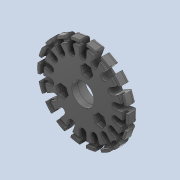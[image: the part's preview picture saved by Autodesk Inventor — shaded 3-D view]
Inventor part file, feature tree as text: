
AUTODESK INVENTOR PART (.ipt)
format: ipt  version: 2020.4 (Build 244396000, 396)  size: 671,232 bytes
history: native  units: mm
features: sketch x8, extrude x7, hole x1, fillet x1
ambient origin geometry x8: Origin, YZ Plane, XZ Plane, XY Plane, X Axis, Y Axis, Z Axis, Center Point
bodies: Solid1 (feature_tree)
feature tree (17):
  extrude  "PartA Base"  Depth=7.0mm TaperAngle=0.0deg
  extrude  "Shaft Entrance"  Depth=2.0mm TaperAngle=0.0deg
  extrude  "Roller Entrance"  TaperAngle=90.0deg  [1 undecoded]
  extrude  "Wire Entrance"  TaperAngle=0.0deg  [1 undecoded]
  hole  "Bearing Fit"  [1 undecoded]
  extrude  "Threads and Gear Fit"  Depth=40.8mm
  extrude  "M3 Nut"  Depth=42.52mm
  fillet  "Wire and Ground Rounding"  Radius=2.1mm
  extrude  "Extrusion7"  Depth=10.0mm
  sketch  "Sketch1"  dims[d0=45.0mm d1=7.0mm d2=0.0mm]
  sketch  "Sketch2"  dims[d3=27.0mm d4=2.0mm d5=0.0mm]
  sketch  "Sketch3"  dims[d6=6.7mm d7=90.0deg]
  sketch  "Sketch4"  dims[d8=3.2mm d9=0.0mm]
  sketch  "Sketch5"  dims[d10=19.6mm d11=10.0mm d12=0.0mm]
  sketch  "Sketch6"  dims[d13=180.0mm d15=360.0deg d17=40.8mm]
  sketch  "Sketch7"  dims[d18=39.08mm d19=42.52mm d20=2.1mm d21=0.0mm]
  sketch  "Sketch8"  dims[d22=11.0mm d23=6.0mm d24=4.0mm d25=2.0mm d26=90.0deg d27=3.0mm d28=0.0mm d29=3.0mm d30=1.91013mm d31=10.833mm d32=30.0mm d34=360.0deg d36=12.0mm d37=10.0mm d38=0.0mm d39=2.76mm d40=2.76mm d41=2.76mm d42=2.55mm d43=0.0mm d44=2.0mm d45=0.625mm d46=12.0mm d47=10.0mm d48=0.0mm]
note: 3 required parameter values undecoded (feature->parameter linkage not recoverable at this tier; creation-order binding heuristic only, values carry confidence <= 0.55)
